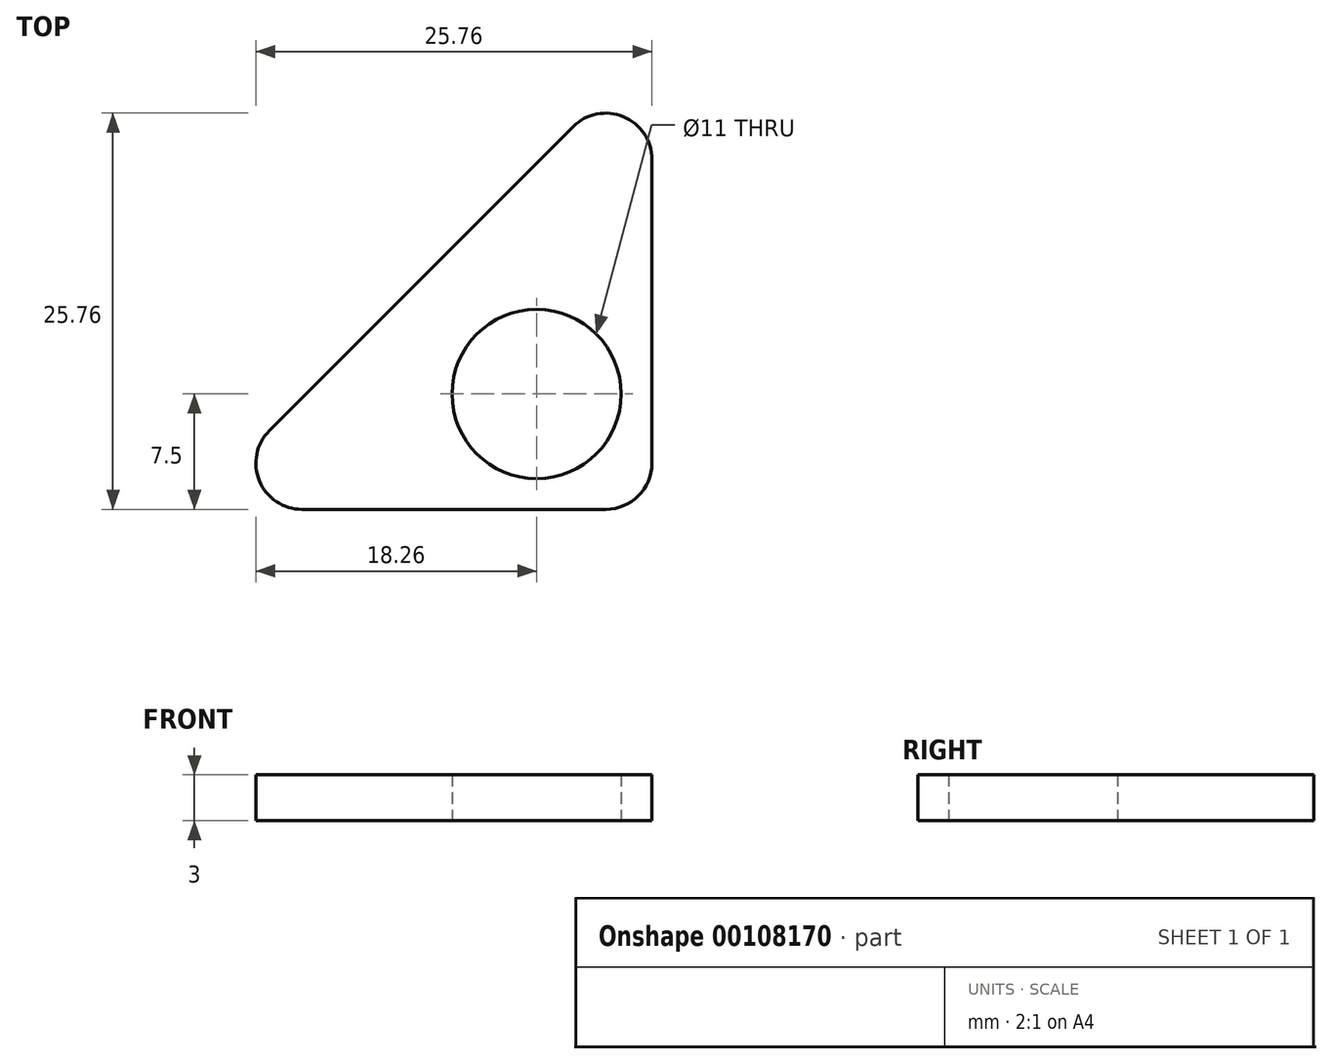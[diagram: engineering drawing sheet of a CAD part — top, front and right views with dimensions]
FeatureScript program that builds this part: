
annotation { "Feature Type Name" : "Feature", "Feature Type Description" : "" }
export const myFeature = defineFeature(function(context is Context, id is Id, definition is map)
    precondition{}
    {
        {
            var Q0;
            Q0=qCreatedBy(makeId("Top.planeOp"),FACE);
            var sketch = newSketch(context, id + "F0", { "sketchPlane" : qUnion([Q0])});
            skCircle(sketch, "E0", {"center": v(0, 0) * mm, "radius": 5.5 * mm});
            skLineSegment(sketch, "E1", {"start": v(7.5, 22.5) * mm, "end": v(7.5, -7.5) * mm});
            skLineSegment(sketch, "E2", {"start": v(7.5, -7.5) * mm, "end": v(-22.5, -7.5) * mm});
            skLineSegment(sketch, "E3", {"start": v(-22.5, -7.5) * mm, "end": v(7.5, 22.5) * mm});
            skLineSegment(sketch, "E4", {"start": v(7.5, -7.5) * mm, "end": v(-7.5, 7.5) * mm, "construction": true});
            skSolve(sketch);
        }
        {
            var Q0;
            Q0 = qSketchRegion(id + "F0", true);
            extrude(context, id + "F1", {"entities" : qUnion([Q0]), "depth" : 3 * mm});
        }
        {
            var Q0;
            Q0=makeQuery(id+"F1.opExtrude","SWEPT_EDGE",EDGE,{"disambiguationData":[OSD([sQuery(id+"F0.wireOp",EDGE,"E2"),sQuery(id+"F0.wireOp",EDGE,"E3")])]});
            var Q1;
            Q1=makeQuery(id+"F1.opExtrude","SWEPT_EDGE",EDGE,{"disambiguationData":[OSD([sQuery(id+"F0.wireOp",EDGE,"E1"),sQuery(id+"F0.wireOp",EDGE,"E2")])]});
            var Q2;
            Q2=makeQuery(id+"F1.opExtrude","SWEPT_EDGE",EDGE,{"disambiguationData":[OSD([sQuery(id+"F0.wireOp",EDGE,"E1"),sQuery(id+"F0.wireOp",EDGE,"E3")])]});
            fillet(context, id + "F2", {"entities" : qUnion([Q0, Q1, Q2]), "radius" : 3 * mm, "tangentPropagation" : true, "allowEdgeOverflow" : false});
        }
    });
